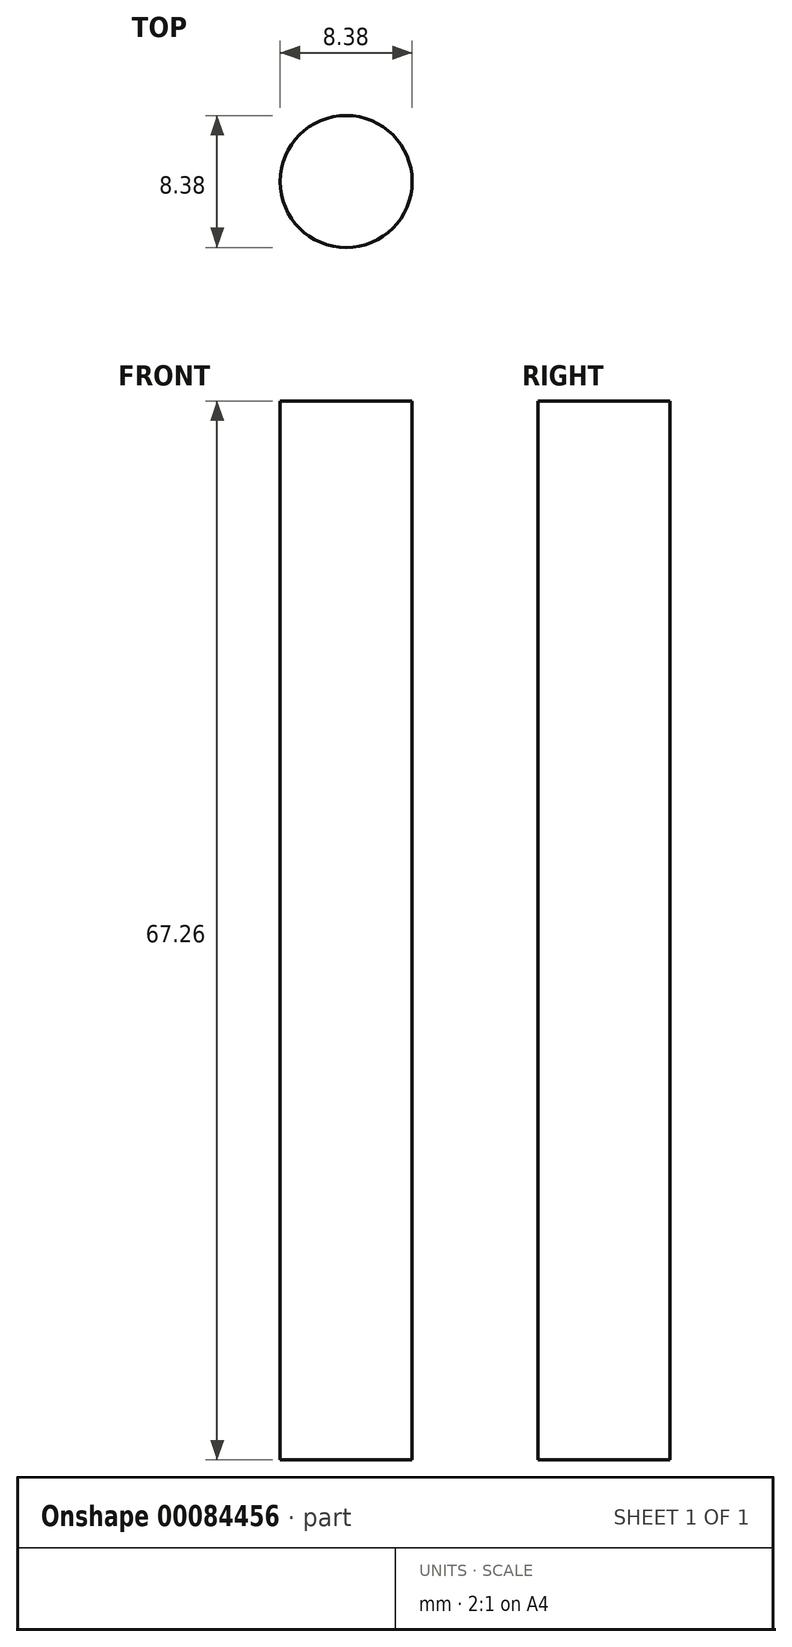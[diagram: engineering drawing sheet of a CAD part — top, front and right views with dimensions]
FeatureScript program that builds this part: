
annotation { "Feature Type Name" : "Feature", "Feature Type Description" : "" }
export const myFeature = defineFeature(function(context is Context, id is Id, definition is map)
    precondition{}
    {
        {
            var Q0;
            Q0=qCreatedBy(makeId("Top.planeOp"),FACE);
            var sketch = newSketch(context, id + "F0", { "sketchPlane" : qUnion([Q0])});
            skCircle(sketch, "E0", {"center": v(0, 0) * mm, "radius": 4.2 * mm});
            skSolve(sketch);
        }
        {
            var Q0;
            Q0=makeQuery(id+"F0.imprint","IMPRINT",FACE,{"disambiguationData":[TD([[makeQuery(id+"F0.imprint","IMPRINT",EDGE,{"derivedFrom":sQuery(id+"F0.wireOp",EDGE,"E0")}),1.0]])]});
            extrude(context, id + "F1", {"entities" : qUnion([Q0]), "depth" : 67.26 * mm});
        }
    });
